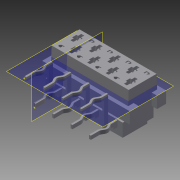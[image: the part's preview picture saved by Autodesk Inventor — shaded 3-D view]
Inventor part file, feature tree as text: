
AUTODESK INVENTOR PART (.ipt)
format: ipt  version: 2014 (Build 180170000, 170)  size: 598,528 bytes
history: native  units: mm
features: other x3, plane x2, imported_body x1
ambient origin geometry x8: Origin, YZ Plane, XZ Plane, XY Plane, X Axis, Y Axis, Z Axis, Center Point
bodies: Volumenkörper1 (feature_tree)
feature tree (6):
  other  "c-215460-8-h-3d1"
  other  "Arbeitspunkt1"
  plane  "Arbeitsebene1"
  other  "Arbeitspunkt3"
  plane  "Arbeitsebene2"
  imported_body  "Basis1"
